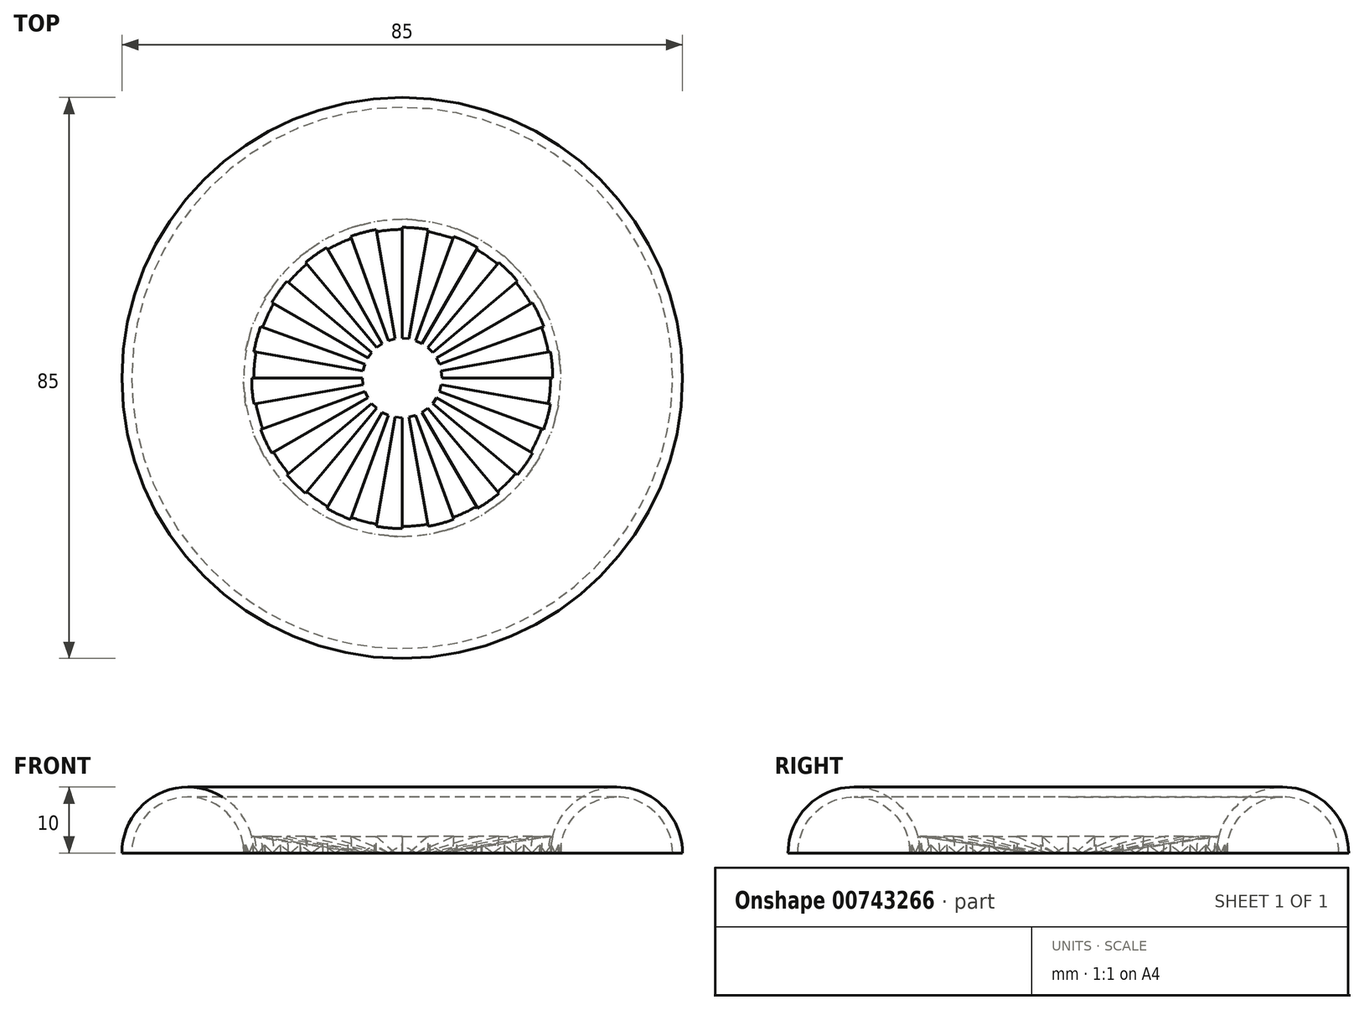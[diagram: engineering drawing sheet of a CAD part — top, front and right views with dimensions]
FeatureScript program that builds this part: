
annotation { "Feature Type Name" : "Feature", "Feature Type Description" : "" }
export const myFeature = defineFeature(function(context is Context, id is Id, definition is map)
    precondition{}
    {
        {
            var Q0;
            Q0=qCreatedBy(makeId("Top.planeOp"),FACE);
            var sketch = newSketch(context, id + "F0", { "sketchPlane" : qUnion([Q0])});
            skCircle(sketch, "E0", {"center": v(0, 0) * mm, "radius": 22.5 * mm});
            skCircle(sketch, "E1", {"center": v(0, 0) * mm, "radius": 24 * mm});
            skSolve(sketch);
        }
        {
            var Q0;
            Q0=qCreatedBy(makeId("Right.planeOp"),FACE);
            var sketch = newSketch(context, id + "F1", { "sketchPlane" : qUnion([Q0])});
            skArc(sketch, "E2", {"start": v(-24, 0) * mm, "mid": v(-32.5, 8.5) * mm, "end": v(-41, 0) * mm});
            skLineSegment(sketch, "E3", {"start": v(-24, 0) * mm, "end": v(-22.5, 0) * mm});
            skLineSegment(sketch, "E4", {"start": v(-41, 0) * mm, "end": v(-42.5, 0) * mm});
            skArc(sketch, "E5", {"start": v(-22.5, 0) * mm, "mid": v(-32.5, 10) * mm, "end": v(-42.5, 0) * mm});
            skLineSegment(sketch, "E6", {"start": v(0, 0) * mm, "end": v(0, 24.3) * mm, "construction": true});
            skSolve(sketch);
        }
        {
            var Q0;
            Q0=makeQuery(id+"F1.imprint","IMPRINT",FACE,{"disambiguationData":[TD([[makeQuery(id+"F1.imprint","IMPRINT",EDGE,{"derivedFrom":sQuery(id+"F1.wireOp",EDGE,"E2")}),-1.0]])]});
            var Q1;
            Q1=sQuery(id+"F1.wireOp",EDGE,"E6");
            revolve(context, id + "F2", {"surfaceOperationType" : NewSurfaceOperationType.NEW, "entities" : qUnion([Q0]), "axis" : qUnion([Q1]), "revolveType" : RevolveType.FULL});
        }
        {
            var Q0;
            Q0=qCreatedBy(makeId("Top.planeOp"),FACE);
            var sketch = newSketch(context, id + "F3", { "sketchPlane" : qUnion([Q0])});
            skCircle(sketch, "E7.cCircle", {"center": v(0, 0) * mm, "radius": 24 * mm, "construction": true});
            skLineSegment(sketch, "E7.0", {"start": v(-4.18, 23.73) * mm, "end": v(0, 24.1) * mm});
            skLineSegment(sketch, "E7.1", {"start": v(0, 24.1) * mm, "end": v(4.18, 23.73) * mm});
            skLineSegment(sketch, "E7.2", {"start": v(4.18, 23.73) * mm, "end": v(8.24, 22.64) * mm});
            skLineSegment(sketch, "E7.3", {"start": v(8.24, 22.64) * mm, "end": v(12.05, 20.86) * mm});
            skLineSegment(sketch, "E7.4", {"start": v(12.05, 20.86) * mm, "end": v(15.49, 18.46) * mm});
            skLineSegment(sketch, "E7.5", {"start": v(15.49, 18.46) * mm, "end": v(18.46, 15.49) * mm});
            skLineSegment(sketch, "E7.6", {"start": v(18.46, 15.49) * mm, "end": v(20.86, 12.05) * mm});
            skLineSegment(sketch, "E7.7", {"start": v(20.86, 12.05) * mm, "end": v(22.64, 8.24) * mm});
            skLineSegment(sketch, "E7.8", {"start": v(22.64, 8.24) * mm, "end": v(23.73, 4.18) * mm});
            skLineSegment(sketch, "E7.9", {"start": v(23.73, 4.18) * mm, "end": v(24.1, 0) * mm});
            skLineSegment(sketch, "E7.10", {"start": v(24.1, 0) * mm, "end": v(23.73, -4.18) * mm});
            skLineSegment(sketch, "E7.11", {"start": v(23.73, -4.18) * mm, "end": v(22.64, -8.24) * mm});
            skLineSegment(sketch, "E7.12", {"start": v(22.64, -8.24) * mm, "end": v(20.86, -12.05) * mm});
            skLineSegment(sketch, "E7.13", {"start": v(20.86, -12.05) * mm, "end": v(18.46, -15.49) * mm});
            skLineSegment(sketch, "E7.14", {"start": v(18.46, -15.49) * mm, "end": v(15.49, -18.46) * mm});
            skLineSegment(sketch, "E7.15", {"start": v(15.49, -18.46) * mm, "end": v(12.05, -20.86) * mm});
            skLineSegment(sketch, "E7.16", {"start": v(12.05, -20.86) * mm, "end": v(8.24, -22.64) * mm});
            skLineSegment(sketch, "E7.17", {"start": v(8.24, -22.64) * mm, "end": v(4.18, -23.73) * mm});
            skLineSegment(sketch, "E7.18", {"start": v(4.18, -23.73) * mm, "end": v(0, -24.1) * mm});
            skLineSegment(sketch, "E7.19", {"start": v(0, -24.1) * mm, "end": v(-4.18, -23.73) * mm});
            skLineSegment(sketch, "E7.20", {"start": v(-4.18, -23.73) * mm, "end": v(-8.24, -22.64) * mm});
            skLineSegment(sketch, "E7.21", {"start": v(-8.24, -22.64) * mm, "end": v(-12.05, -20.86) * mm});
            skLineSegment(sketch, "E7.22", {"start": v(-12.05, -20.86) * mm, "end": v(-15.49, -18.46) * mm});
            skLineSegment(sketch, "E7.23", {"start": v(-15.49, -18.46) * mm, "end": v(-18.46, -15.49) * mm});
            skLineSegment(sketch, "E7.24", {"start": v(-18.46, -15.49) * mm, "end": v(-20.86, -12.05) * mm});
            skLineSegment(sketch, "E7.25", {"start": v(-20.86, -12.05) * mm, "end": v(-22.64, -8.24) * mm});
            skLineSegment(sketch, "E7.26", {"start": v(-22.64, -8.24) * mm, "end": v(-23.73, -4.18) * mm});
            skLineSegment(sketch, "E7.27", {"start": v(-23.73, -4.18) * mm, "end": v(-24.1, 0) * mm});
            skLineSegment(sketch, "E7.28", {"start": v(-24.1, 0) * mm, "end": v(-23.73, 4.18) * mm});
            skLineSegment(sketch, "E7.29", {"start": v(-23.73, 4.18) * mm, "end": v(-22.64, 8.24) * mm});
            skLineSegment(sketch, "E7.30", {"start": v(-22.64, 8.24) * mm, "end": v(-20.86, 12.05) * mm});
            skLineSegment(sketch, "E7.31", {"start": v(-20.86, 12.05) * mm, "end": v(-18.46, 15.49) * mm});
            skLineSegment(sketch, "E7.32", {"start": v(-18.46, 15.49) * mm, "end": v(-15.49, 18.46) * mm});
            skLineSegment(sketch, "E7.33", {"start": v(-15.49, 18.46) * mm, "end": v(-12.05, 20.86) * mm});
            skLineSegment(sketch, "E7.34", {"start": v(-12.05, 20.86) * mm, "end": v(-8.24, 22.64) * mm});
            skLineSegment(sketch, "E7.35", {"start": v(-8.24, 22.64) * mm, "end": v(-4.18, 23.73) * mm});
            skPoint(sketch, "E7.0.midPoint", {"position": v(-2.1, 23.9) * mm});
            skCircle(sketch, "E8.cCircle", {"center": v(0, 0) * mm, "radius": 6 * mm, "construction": true});
            skLineSegment(sketch, "E8.0", {"start": v(3.87, 4.61) * mm, "end": v(4.61, 3.87) * mm});
            skLineSegment(sketch, "E8.1", {"start": v(4.61, 3.87) * mm, "end": v(5.22, 3.01) * mm});
            skLineSegment(sketch, "E8.2", {"start": v(5.22, 3.01) * mm, "end": v(5.66, 2.06) * mm});
            skLineSegment(sketch, "E8.3", {"start": v(5.66, 2.06) * mm, "end": v(5.93, 1.05) * mm});
            skLineSegment(sketch, "E8.4", {"start": v(5.93, 1.05) * mm, "end": v(6.02, 0) * mm});
            skLineSegment(sketch, "E8.5", {"start": v(6.02, 0) * mm, "end": v(5.93, -1.05) * mm});
            skLineSegment(sketch, "E8.6", {"start": v(5.93, -1.05) * mm, "end": v(5.66, -2.06) * mm});
            skLineSegment(sketch, "E8.7", {"start": v(5.66, -2.06) * mm, "end": v(5.22, -3.01) * mm});
            skLineSegment(sketch, "E8.8", {"start": v(5.22, -3.01) * mm, "end": v(4.61, -3.87) * mm});
            skLineSegment(sketch, "E8.9", {"start": v(4.61, -3.87) * mm, "end": v(3.87, -4.61) * mm});
            skLineSegment(sketch, "E8.10", {"start": v(3.87, -4.61) * mm, "end": v(3.01, -5.22) * mm});
            skLineSegment(sketch, "E8.11", {"start": v(3.01, -5.22) * mm, "end": v(2.06, -5.66) * mm});
            skLineSegment(sketch, "E8.12", {"start": v(2.06, -5.66) * mm, "end": v(1.05, -5.93) * mm});
            skLineSegment(sketch, "E8.13", {"start": v(1.05, -5.93) * mm, "end": v(0, -6.02) * mm});
            skLineSegment(sketch, "E8.14", {"start": v(0, -6.02) * mm, "end": v(-1.05, -5.93) * mm});
            skLineSegment(sketch, "E8.15", {"start": v(-1.05, -5.93) * mm, "end": v(-2.06, -5.66) * mm});
            skLineSegment(sketch, "E8.16", {"start": v(-2.06, -5.66) * mm, "end": v(-3.01, -5.22) * mm});
            skLineSegment(sketch, "E8.17", {"start": v(-3.01, -5.22) * mm, "end": v(-3.87, -4.61) * mm});
            skLineSegment(sketch, "E8.18", {"start": v(-3.87, -4.61) * mm, "end": v(-4.61, -3.87) * mm});
            skLineSegment(sketch, "E8.19", {"start": v(-4.61, -3.87) * mm, "end": v(-5.22, -3.01) * mm});
            skLineSegment(sketch, "E8.20", {"start": v(-5.22, -3.01) * mm, "end": v(-5.66, -2.06) * mm});
            skLineSegment(sketch, "E8.21", {"start": v(-5.66, -2.06) * mm, "end": v(-5.93, -1.05) * mm});
            skLineSegment(sketch, "E8.22", {"start": v(-5.93, -1.05) * mm, "end": v(-6.02, 0) * mm});
            skLineSegment(sketch, "E8.23", {"start": v(-6.02, 0) * mm, "end": v(-5.93, 1.05) * mm});
            skLineSegment(sketch, "E8.24", {"start": v(-5.93, 1.05) * mm, "end": v(-5.66, 2.06) * mm});
            skLineSegment(sketch, "E8.25", {"start": v(-5.66, 2.06) * mm, "end": v(-5.22, 3.01) * mm});
            skLineSegment(sketch, "E8.26", {"start": v(-5.22, 3.01) * mm, "end": v(-4.61, 3.87) * mm});
            skLineSegment(sketch, "E8.27", {"start": v(-4.61, 3.87) * mm, "end": v(-3.87, 4.61) * mm});
            skLineSegment(sketch, "E8.28", {"start": v(-3.87, 4.61) * mm, "end": v(-3.01, 5.22) * mm});
            skLineSegment(sketch, "E8.29", {"start": v(-3.01, 5.22) * mm, "end": v(-2.06, 5.66) * mm});
            skLineSegment(sketch, "E8.30", {"start": v(-2.06, 5.66) * mm, "end": v(-1.05, 5.93) * mm});
            skLineSegment(sketch, "E8.31", {"start": v(-1.05, 5.93) * mm, "end": v(0, 6.02) * mm});
            skLineSegment(sketch, "E8.32", {"start": v(0, 6.02) * mm, "end": v(1.05, 5.93) * mm});
            skLineSegment(sketch, "E8.33", {"start": v(1.05, 5.93) * mm, "end": v(2.06, 5.66) * mm});
            skLineSegment(sketch, "E8.34", {"start": v(2.06, 5.66) * mm, "end": v(3.01, 5.22) * mm});
            skLineSegment(sketch, "E8.35", {"start": v(3.01, 5.22) * mm, "end": v(3.87, 4.61) * mm});
            skPoint(sketch, "E8.0.midPoint", {"position": v(4.24, 4.24) * mm});
            skLineSegment(sketch, "E9", {"start": v(-22.64, -8.24) * mm, "end": v(-5.66, -2.06) * mm});
            skLineSegment(sketch, "E10", {"start": v(-5.93, -1.05) * mm, "end": v(-23.73, -4.18) * mm});
            skLineSegment(sketch, "E11", {"start": v(-6.02, 0) * mm, "end": v(-24.1, 0) * mm});
            skLineSegment(sketch, "E12", {"start": v(-5.22, -3.01) * mm, "end": v(-20.86, -12.05) * mm});
            skLineSegment(sketch, "E13", {"start": v(-18.46, -15.49) * mm, "end": v(-4.61, -3.87) * mm});
            skLineSegment(sketch, "E14", {"start": v(-3.87, -4.61) * mm, "end": v(-15.49, -18.46) * mm});
            skLineSegment(sketch, "E15", {"start": v(-3.01, -5.22) * mm, "end": v(-12.05, -20.86) * mm});
            skLineSegment(sketch, "E16", {"start": v(-2.06, -5.66) * mm, "end": v(-8.24, -22.64) * mm});
            skLineSegment(sketch, "E17", {"start": v(-23.73, 4.18) * mm, "end": v(-5.93, 1.05) * mm});
            skLineSegment(sketch, "E18", {"start": v(-5.66, 2.06) * mm, "end": v(-22.64, 8.24) * mm});
            skLineSegment(sketch, "E19", {"start": v(-20.86, 12.05) * mm, "end": v(-5.22, 3.01) * mm});
            skLineSegment(sketch, "E20", {"start": v(-4.61, 3.87) * mm, "end": v(-18.46, 15.49) * mm});
            skLineSegment(sketch, "E21", {"start": v(-15.49, 18.46) * mm, "end": v(-3.87, 4.61) * mm});
            skLineSegment(sketch, "E22", {"start": v(-3.01, 5.22) * mm, "end": v(-12.05, 20.86) * mm});
            skLineSegment(sketch, "E23", {"start": v(-8.24, 22.64) * mm, "end": v(-2.06, 5.66) * mm});
            skLineSegment(sketch, "E24", {"start": v(-1.05, 5.93) * mm, "end": v(-4.18, 23.73) * mm});
            skLineSegment(sketch, "E25", {"start": v(0, 24.1) * mm, "end": v(0, 6.02) * mm});
            skLineSegment(sketch, "E26", {"start": v(1.05, 5.93) * mm, "end": v(4.18, 23.73) * mm});
            skLineSegment(sketch, "E27", {"start": v(8.24, 22.64) * mm, "end": v(2.06, 5.66) * mm});
            skLineSegment(sketch, "E28", {"start": v(3.01, 5.22) * mm, "end": v(12.05, 20.86) * mm});
            skLineSegment(sketch, "E29", {"start": v(15.49, 18.46) * mm, "end": v(3.87, 4.61) * mm});
            skLineSegment(sketch, "E30", {"start": v(4.61, 3.87) * mm, "end": v(18.46, 15.49) * mm});
            skLineSegment(sketch, "E31", {"start": v(20.86, 12.05) * mm, "end": v(5.22, 3.01) * mm});
            skLineSegment(sketch, "E32", {"start": v(5.66, 2.06) * mm, "end": v(22.64, 8.24) * mm});
            skLineSegment(sketch, "E33", {"start": v(23.73, 4.18) * mm, "end": v(5.93, 1.05) * mm});
            skLineSegment(sketch, "E34", {"start": v(6.02, 0) * mm, "end": v(24.1, 0) * mm});
            skLineSegment(sketch, "E35", {"start": v(23.73, -4.18) * mm, "end": v(5.93, -1.05) * mm});
            skLineSegment(sketch, "E36", {"start": v(5.66, -2.06) * mm, "end": v(22.64, -8.24) * mm});
            skLineSegment(sketch, "E37", {"start": v(20.86, -12.05) * mm, "end": v(5.22, -3.01) * mm});
            skLineSegment(sketch, "E38", {"start": v(4.61, -3.87) * mm, "end": v(18.46, -15.49) * mm});
            skLineSegment(sketch, "E39", {"start": v(15.49, -18.46) * mm, "end": v(3.87, -4.61) * mm});
            skLineSegment(sketch, "E40", {"start": v(3.01, -5.22) * mm, "end": v(12.05, -20.86) * mm});
            skLineSegment(sketch, "E41", {"start": v(8.24, -22.64) * mm, "end": v(2.06, -5.66) * mm});
            skLineSegment(sketch, "E42", {"start": v(1.05, -5.93) * mm, "end": v(4.18, -23.73) * mm});
            skLineSegment(sketch, "E43", {"start": v(0, -24.1) * mm, "end": v(0, -6.02) * mm});
            skLineSegment(sketch, "E44", {"start": v(-1.05, -5.93) * mm, "end": v(-4.18, -23.73) * mm});
            skLineSegment(sketch, "E45", {"start": v(0, 0) * mm, "end": v(0, 60.3) * mm, "construction": true});
            skSolve(sketch);
        }
        {
            var Q0;
            Q0=makeQuery(id+"F3.imprint","IMPRINT",FACE,{"disambiguationData":[TD([[makeQuery(id+"F3.imprint","IMPRINT",EDGE,{"derivedFrom":sQuery(id+"F3.wireOp",EDGE,"E7.25")}),-1.0]])]});
            var Q1;
            Q1=makeQuery(id+"F3.imprint","IMPRINT",FACE,{"disambiguationData":[TD([[makeQuery(id+"F3.imprint","IMPRINT",EDGE,{"derivedFrom":sQuery(id+"F3.wireOp",EDGE,"E7.27")}),-1.0]])]});
            var Q2;
            Q2=makeQuery(id+"F3.imprint","IMPRINT",FACE,{"disambiguationData":[TD([[makeQuery(id+"F3.imprint","IMPRINT",EDGE,{"derivedFrom":sQuery(id+"F3.wireOp",EDGE,"E7.29")}),-1.0]])]});
            var Q3;
            Q3=makeQuery(id+"F3.imprint","IMPRINT",FACE,{"disambiguationData":[TD([[makeQuery(id+"F3.imprint","IMPRINT",EDGE,{"derivedFrom":sQuery(id+"F3.wireOp",EDGE,"E7.31")}),-1.0]])]});
            var Q4;
            Q4=makeQuery(id+"F3.imprint","IMPRINT",FACE,{"disambiguationData":[TD([[makeQuery(id+"F3.imprint","IMPRINT",EDGE,{"derivedFrom":sQuery(id+"F3.wireOp",EDGE,"E7.33")}),-1.0]])]});
            var Q5;
            Q5=makeQuery(id+"F3.imprint","IMPRINT",FACE,{"disambiguationData":[TD([[makeQuery(id+"F3.imprint","IMPRINT",EDGE,{"derivedFrom":sQuery(id+"F3.wireOp",EDGE,"E7.23")}),-1.0]])]});
            var Q6;
            Q6=makeQuery(id+"F3.imprint","IMPRINT",FACE,{"disambiguationData":[TD([[makeQuery(id+"F3.imprint","IMPRINT",EDGE,{"derivedFrom":sQuery(id+"F3.wireOp",EDGE,"E7.21")}),-1.0]])]});
            var Q7;
            Q7=makeQuery(id+"F3.imprint","IMPRINT",FACE,{"disambiguationData":[TD([[makeQuery(id+"F3.imprint","IMPRINT",EDGE,{"derivedFrom":sQuery(id+"F3.wireOp",EDGE,"E7.19")}),-1.0]])]});
            var Q8;
            Q8=makeQuery(id+"F3.imprint","IMPRINT",FACE,{"disambiguationData":[TD([[makeQuery(id+"F3.imprint","IMPRINT",EDGE,{"derivedFrom":sQuery(id+"F3.wireOp",EDGE,"E7.17")}),-1.0]])]});
            var Q9;
            Q9=makeQuery(id+"F3.imprint","IMPRINT",FACE,{"disambiguationData":[TD([[makeQuery(id+"F3.imprint","IMPRINT",EDGE,{"derivedFrom":sQuery(id+"F3.wireOp",EDGE,"E7.15")}),-1.0]])]});
            var Q10;
            Q10=makeQuery(id+"F3.imprint","IMPRINT",FACE,{"disambiguationData":[TD([[makeQuery(id+"F3.imprint","IMPRINT",EDGE,{"derivedFrom":sQuery(id+"F3.wireOp",EDGE,"E7.13")}),-1.0]])]});
            var Q11;
            Q11=makeQuery(id+"F3.imprint","IMPRINT",FACE,{"disambiguationData":[TD([[makeQuery(id+"F3.imprint","IMPRINT",EDGE,{"derivedFrom":sQuery(id+"F3.wireOp",EDGE,"E7.11")}),-1.0]])]});
            var Q12;
            Q12=makeQuery(id+"F3.imprint","IMPRINT",FACE,{"disambiguationData":[TD([[makeQuery(id+"F3.imprint","IMPRINT",EDGE,{"derivedFrom":sQuery(id+"F3.wireOp",EDGE,"E7.9")}),-1.0]])]});
            var Q13;
            Q13=makeQuery(id+"F3.imprint","IMPRINT",FACE,{"disambiguationData":[TD([[makeQuery(id+"F3.imprint","IMPRINT",EDGE,{"derivedFrom":sQuery(id+"F3.wireOp",EDGE,"E7.7")}),-1.0]])]});
            var Q14;
            Q14=makeQuery(id+"F3.imprint","IMPRINT",FACE,{"disambiguationData":[TD([[makeQuery(id+"F3.imprint","IMPRINT",EDGE,{"derivedFrom":sQuery(id+"F3.wireOp",EDGE,"E7.5")}),-1.0]])]});
            var Q15;
            Q15=makeQuery(id+"F3.imprint","IMPRINT",FACE,{"disambiguationData":[TD([[makeQuery(id+"F3.imprint","IMPRINT",EDGE,{"derivedFrom":sQuery(id+"F3.wireOp",EDGE,"E7.3")}),-1.0]])]});
            var Q16;
            Q16=makeQuery(id+"F3.imprint","IMPRINT",FACE,{"disambiguationData":[TD([[makeQuery(id+"F3.imprint","IMPRINT",EDGE,{"derivedFrom":sQuery(id+"F3.wireOp",EDGE,"E7.1")}),-1.0]])]});
            var Q17;
            Q17=makeQuery(id+"F3.imprint","IMPRINT",FACE,{"disambiguationData":[TD([[makeQuery(id+"F3.imprint","IMPRINT",EDGE,{"derivedFrom":sQuery(id+"F3.wireOp",EDGE,"E7.35")}),-1.0]])]});
            extrude(context, id + "F4", {"entities" : qUnion([Q0, Q1, Q2, Q3, Q4, Q5, Q6, Q7, Q8, Q9, Q10, Q11, Q12, Q13, Q14, Q15, Q16, Q17]), "operationType" : NewBodyOperationType.ADD, "depth" : 3 * mm, "offsetDistance" : 25 * mm});
        }
        {
            var Q0;
            Q0=makeQuery(id+"F4.opExtrude","CAP_EDGE",EDGE,{"disambiguationData":[OSD([sQuery(id+"F3.wireOp",EDGE,"E8.22")])],"isStart":false});
            var Q1;
            Q1=makeQuery(id+"F4.opExtrude","CAP_EDGE",EDGE,{"disambiguationData":[OSD([sQuery(id+"F3.wireOp",EDGE,"E8.24")])],"isStart":false});
            var Q2;
            Q2=makeQuery(id+"F4.opExtrude","CAP_EDGE",EDGE,{"disambiguationData":[OSD([sQuery(id+"F3.wireOp",EDGE,"E8.26")])],"isStart":false});
            var Q3;
            Q3=makeQuery(id+"F4.opExtrude","CAP_EDGE",EDGE,{"disambiguationData":[OSD([sQuery(id+"F3.wireOp",EDGE,"E8.28")])],"isStart":false});
            var Q4;
            Q4=makeQuery(id+"F4.opExtrude","CAP_EDGE",EDGE,{"disambiguationData":[OSD([sQuery(id+"F3.wireOp",EDGE,"E8.30")])],"isStart":false});
            var Q5;
            Q5=makeQuery(id+"F4.opExtrude","CAP_EDGE",EDGE,{"disambiguationData":[OSD([sQuery(id+"F3.wireOp",EDGE,"E8.32")])],"isStart":false});
            var Q6;
            Q6=makeQuery(id+"F4.opExtrude","CAP_EDGE",EDGE,{"disambiguationData":[OSD([sQuery(id+"F3.wireOp",EDGE,"E8.34")])],"isStart":false});
            var Q7;
            Q7=makeQuery(id+"F4.opExtrude","CAP_EDGE",EDGE,{"disambiguationData":[OSD([sQuery(id+"F3.wireOp",EDGE,"E8.0")])],"isStart":false});
            var Q8;
            Q8=makeQuery(id+"F4.opExtrude","CAP_EDGE",EDGE,{"disambiguationData":[OSD([sQuery(id+"F3.wireOp",EDGE,"E8.2")])],"isStart":false});
            var Q9;
            Q9=makeQuery(id+"F4.opExtrude","CAP_EDGE",EDGE,{"disambiguationData":[OSD([sQuery(id+"F3.wireOp",EDGE,"E8.4")])],"isStart":false});
            var Q10;
            Q10=makeQuery(id+"F4.opExtrude","CAP_EDGE",EDGE,{"disambiguationData":[OSD([sQuery(id+"F3.wireOp",EDGE,"E8.6")])],"isStart":false});
            var Q11;
            Q11=makeQuery(id+"F4.opExtrude","CAP_EDGE",EDGE,{"disambiguationData":[OSD([sQuery(id+"F3.wireOp",EDGE,"E8.8")])],"isStart":false});
            var Q12;
            Q12=makeQuery(id+"F4.opExtrude","CAP_EDGE",EDGE,{"disambiguationData":[OSD([sQuery(id+"F3.wireOp",EDGE,"E8.10")])],"isStart":false});
            var Q13;
            Q13=makeQuery(id+"F4.opExtrude","CAP_EDGE",EDGE,{"disambiguationData":[OSD([sQuery(id+"F3.wireOp",EDGE,"E8.12")])],"isStart":false});
            var Q14;
            Q14=makeQuery(id+"F4.opExtrude","CAP_EDGE",EDGE,{"disambiguationData":[OSD([sQuery(id+"F3.wireOp",EDGE,"E8.14")])],"isStart":false});
            var Q15;
            Q15=makeQuery(id+"F4.opExtrude","CAP_EDGE",EDGE,{"disambiguationData":[OSD([sQuery(id+"F3.wireOp",EDGE,"E8.16")])],"isStart":false});
            var Q16;
            Q16=makeQuery(id+"F4.opExtrude","CAP_EDGE",EDGE,{"disambiguationData":[OSD([sQuery(id+"F3.wireOp",EDGE,"E8.18")])],"isStart":false});
            var Q17;
            Q17=makeQuery(id+"F4.opExtrude","CAP_EDGE",EDGE,{"disambiguationData":[OSD([sQuery(id+"F3.wireOp",EDGE,"E8.20")])],"isStart":false});
            chamfer(context, id + "F5", {"entities" : qUnion([Q0, Q1, Q2, Q3, Q4, Q5, Q6, Q7, Q8, Q9, Q10, Q11, Q12, Q13, Q14, Q15, Q16, Q17]), "chamferType" : ChamferType.TWO_OFFSETS, "width1" : 20 * mm, "oppositeDirection" : false, "width2" : 3 * mm, "tangentPropagation" : true});
        }
    });
